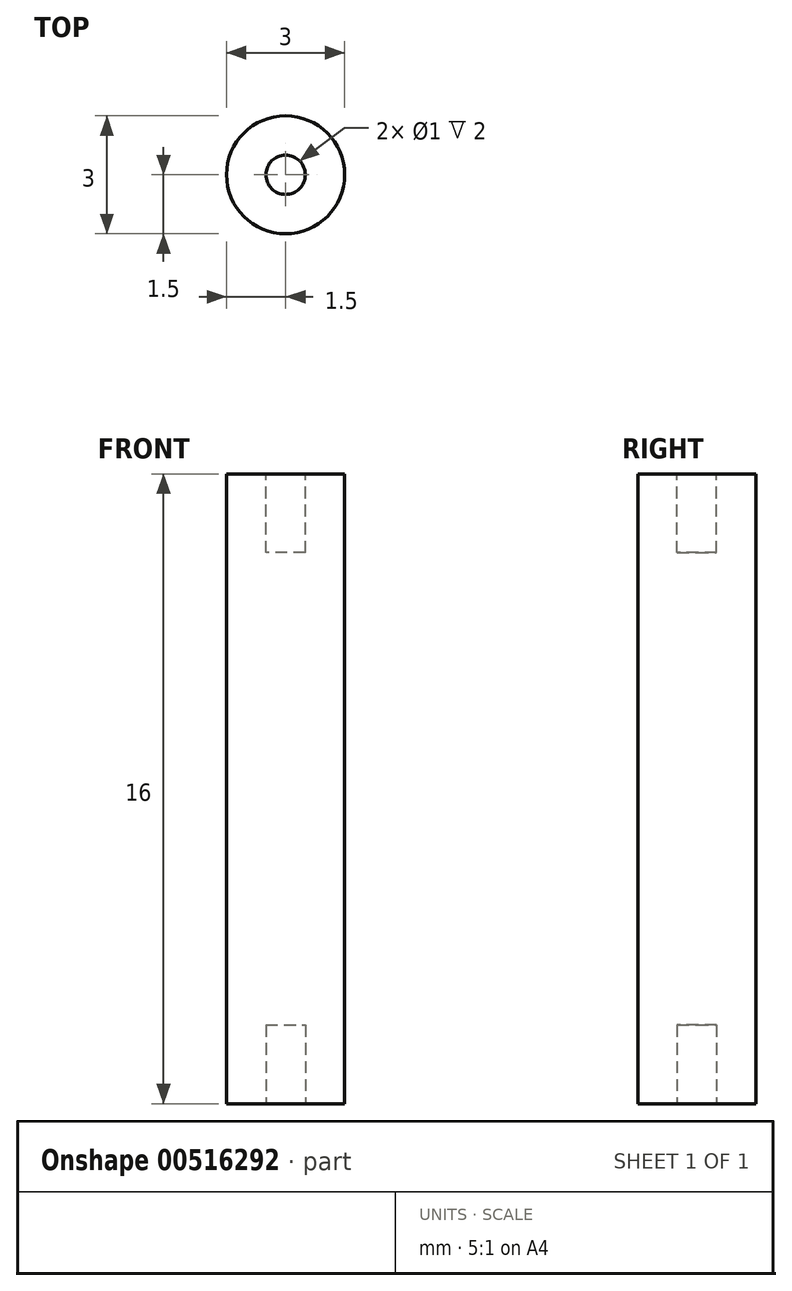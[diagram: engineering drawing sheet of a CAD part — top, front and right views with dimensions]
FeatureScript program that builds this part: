
annotation { "Feature Type Name" : "Feature", "Feature Type Description" : "" }
export const myFeature = defineFeature(function(context is Context, id is Id, definition is map)
    precondition{}
    {
        {
            var Q0;
            Q0=qCreatedBy(makeId("Top.planeOp"),FACE);
            var sketch = newSketch(context, id + "F0", { "sketchPlane" : qUnion([Q0])});
            skCircle(sketch, "E0", {"center": v(0, 0) * mm, "radius": 1.5 * mm});
            skSolve(sketch);
        }
        {
            var Q0;
            Q0 = qSketchRegion(id + "F0", true);
            extrude(context, id + "F1", {"entities" : qUnion([Q0]), "depth" : 16 * mm, "offsetDistance" : 25 * mm});
        }
        {
            var Q0;
            Q0=makeQuery(id+"F1.opExtrude","CAP_FACE",FACE,{"disambiguationData":[OSD([sQuery(id+"F0.wireOp",EDGE,"E0")])],"isStart":false});
            var sketch = newSketch(context, id + "F2", { "sketchPlane" : qUnion([Q0])});
            skCircle(sketch, "E1", {"center": v(0, 0) * mm, "radius": 0.5 * mm});
            skSolve(sketch);
        }
        {
            var Q0;
            Q0 = qSketchRegion(id + "F2", true);
            extrude(context, id + "F3", {"entities" : qUnion([Q0]), "operationType" : NewBodyOperationType.REMOVE, "oppositeDirection" : true, "depth" : 2 * mm, "offsetDistance" : 25 * mm});
        }
        {
            var Q0;
            Q0=makeQuery(id+"F1.opExtrude","CAP_FACE",FACE,{"disambiguationData":[OSD([sQuery(id+"F0.wireOp",EDGE,"E0")])],"isStart":true});
            var sketch = newSketch(context, id + "F4", { "sketchPlane" : qUnion([Q0])});
            skCircle(sketch, "E2", {"center": v(0, 0) * mm, "radius": 0.5 * mm});
            skSolve(sketch);
        }
        {
            var Q0;
            Q0 = qSketchRegion(id + "F4", true);
            extrude(context, id + "F5", {"entities" : qUnion([Q0]), "operationType" : NewBodyOperationType.REMOVE, "oppositeDirection" : true, "depth" : 2 * mm, "offsetDistance" : 25 * mm});
        }
    });
